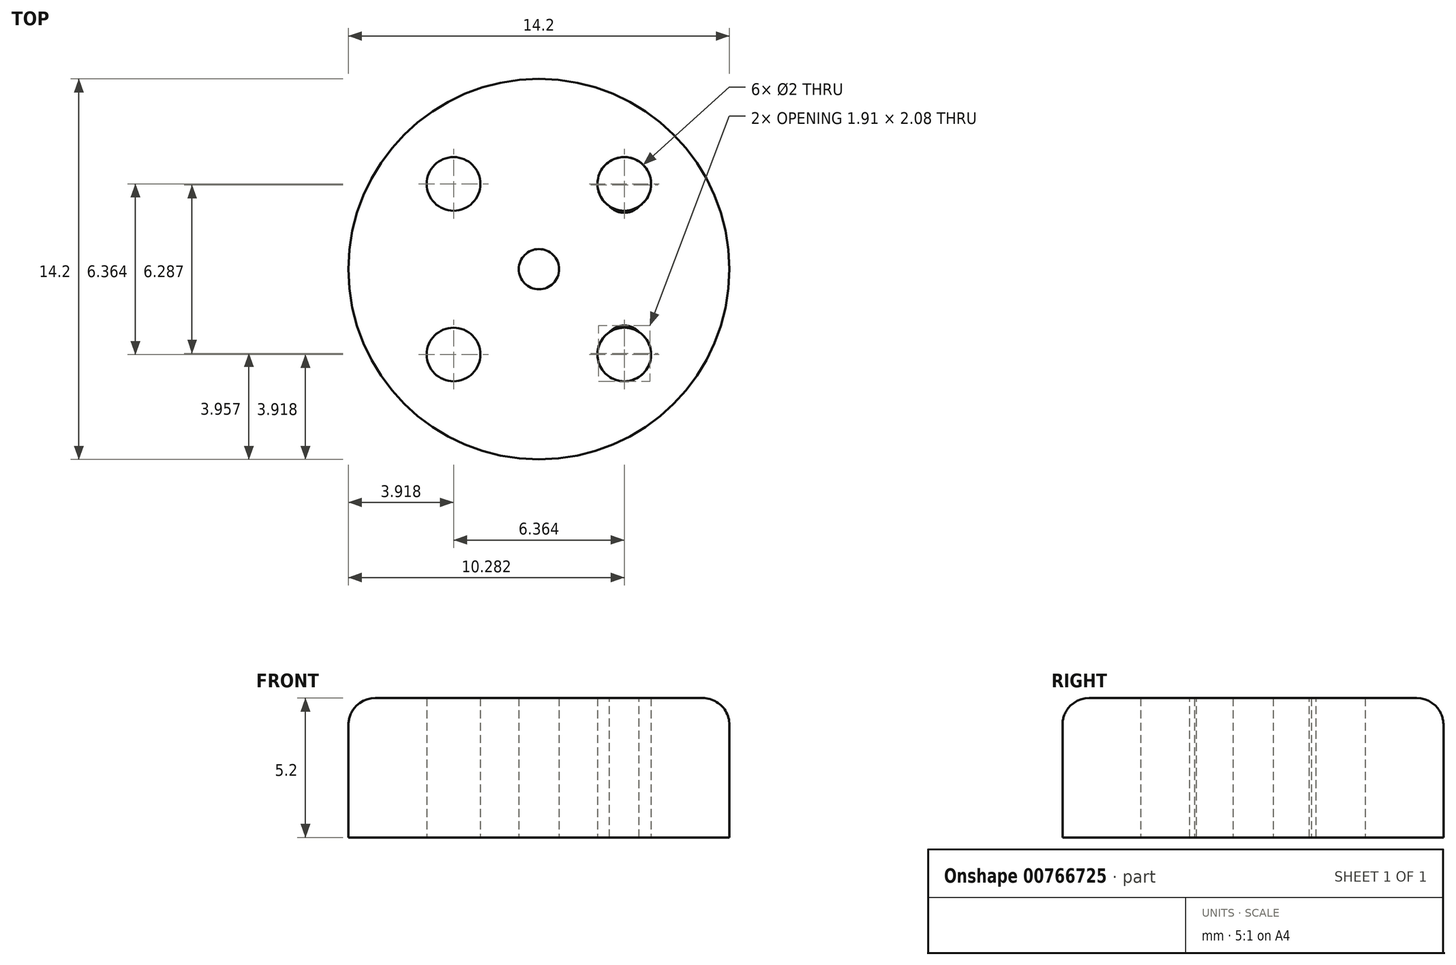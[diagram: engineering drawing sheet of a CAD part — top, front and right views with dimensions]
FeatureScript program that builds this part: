
annotation { "Feature Type Name" : "Feature", "Feature Type Description" : "" }
export const myFeature = defineFeature(function(context is Context, id is Id, definition is map)
    precondition{}
    {
        {
            var Q0;
            Q0=qCreatedBy(makeId("Top.planeOp"),FACE);
            var sketch = newSketch(context, id + "F0", { "sketchPlane" : qUnion([Q0])});
            skCircle(sketch, "E0", {"center": v(0, 0) * mm, "radius": 7.1 * mm});
            skCircle(sketch, "E1", {"center": v(0, 0) * mm, "radius": 0.75 * mm});
            skLineSegment(sketch, "E2.bottom", {"start": v(3.18, 3.18) * mm, "end": v(-3.18, 3.18) * mm, "construction": true});
            skLineSegment(sketch, "E2.top", {"start": v(3.18, -3.18) * mm, "end": v(-3.18, -3.18) * mm, "construction": true});
            skLineSegment(sketch, "E2.left", {"start": v(3.18, 3.18) * mm, "end": v(3.18, -3.18) * mm, "construction": true});
            skLineSegment(sketch, "E2.right", {"start": v(-3.18, 3.18) * mm, "end": v(-3.18, -3.18) * mm, "construction": true});
            skCircle(sketch, "E3", {"center": v(3.18, 3.18) * mm, "radius": 1 * mm});
            skCircle(sketch, "E4", {"center": v(3.18, -3.18) * mm, "radius": 1 * mm});
            skCircle(sketch, "E5", {"center": v(-3.18, -3.18) * mm, "radius": 1 * mm});
            skCircle(sketch, "E6", {"center": v(-3.18, 3.18) * mm, "radius": 1 * mm});
            skSolve(sketch);
        }
        {
            var Q0;
            Q0 = qSketchRegion(id + "F0", true);
            extrude(context, id + "F1", {"entities" : qUnion([Q0]), "depth" : 5.2 * mm, "offsetDistance" : 25 * mm});
        }
        {
            var Q0;
            Q0=makeQuery(id+"F1.opExtrude","CAP_EDGE",EDGE,{"disambiguationData":[OSD([sQuery(id+"F0.wireOp",EDGE,"E0")])],"isStart":false});
            fillet(context, id + "F2", {"entities" : qUnion([Q0]), "radius" : 1 * mm, "tangentPropagation" : true, "allowEdgeOverflow" : false});
        }
        {
            var Q0;
            Q0=qCreatedBy(makeId("Right.planeOp"),FACE);
            var sketch = newSketch(context, id + "F3", { "sketchPlane" : qUnion([Q0])});
            skLineSegment(sketch, "E7", {"start": v(-2.35, 4.95) * mm, "end": v(2.35, 0.25) * mm, "construction": true});
            skLineSegment(sketch, "E8", {"start": v(0, 5.2) * mm, "end": v(0, 0) * mm, "construction": true});
            skPoint(sketch, "E9", {"position": v(0, 2.6) * mm});
            skArc(sketch, "E10.0.startCap", {"start": v(-2.53, 4.77) * mm, "mid": v(-2.53, 5.13) * mm, "end": v(-2.17, 5.13) * mm});
            skArc(sketch, "E10.0.endCap", {"start": v(2.53, 0.43) * mm, "mid": v(2.53, 0.07) * mm, "end": v(2.17, 0.07) * mm});
            skLineSegment(sketch, "E10.0.left", {"start": v(-2.17, 5.13) * mm, "end": v(2.53, 0.43) * mm});
            skLineSegment(sketch, "E10.0.right", {"start": v(-2.53, 4.77) * mm, "end": v(2.17, 0.07) * mm});
            skSolve(sketch);
        }
        {
            var Q0;
            Q0 = qSketchRegion(id + "F3", true);
            extrude(context, id + "F4", {"entities" : qUnion([Q0]), "operationType" : NewBodyOperationType.ADD, "depth" : 2.3 / 50.8 * mm, "offsetDistance" : 25 * mm});
        }
        {
            var Q0;
            {var subQ0=sQuery(id+"F3.wireOp",EDGE,"E10.0.left");Q0=makeQuery(id+"F4.boolean.opBoolean","SPLIT",FACE,{"disambiguationData":[TD([makeQuery(id+"F1.opExtrude","SWEPT_FACE",FACE,{"disambiguationData":[OSD([sQuery(id+"F0.wireOp",EDGE,"E0")])]})])],"derivedFrom":makeQuery(id+"F4.opExtrude","SWEPT_FACE",FACE,{"disambiguationData":[OSD([subQ0])]})});}
            var sketch = newSketch(context, id + "F5", { "sketchPlane" : qUnion([Q0])});
            skLineSegment(sketch, "E11", {"start": v(29.21, -1.84) * mm, "end": v(15.18, -1.84) * mm, "construction": true});
            skLineSegment(sketch, "E12.0", {"start": v(29.21, 1.48) * mm, "end": v(29.21, 1.73) * mm});
            skLineSegment(sketch, "E13", {"start": v(29.21, 1.73) * mm, "end": v(26.83, 1.73) * mm});
            skArc(sketch, "E14", {"start": v(29.2, -0.65) * mm, "mid": v(28.51, 1.04) * mm, "end": v(26.83, 1.73) * mm});
            skLineSegment(sketch, "E15", {"start": v(29.21, 1.48) * mm, "end": v(29.21, -0.65) * mm});
            skLineSegment(sketch, "E16", {"start": v(29.21, -0.65) * mm, "end": v(29.21, -3.03) * mm, "construction": true});
            skArc(sketch, "E17.MirrorCS", {"start": v(29.2, -3.03) * mm, "mid": v(28.51, -4.71) * mm, "end": v(26.83, -5.41) * mm});
            skLineSegment(sketch, "E18.MirrorCS", {"start": v(29.21, -5.41) * mm, "end": v(26.83, -5.41) * mm});
            skLineSegment(sketch, "E19.MirrorCS", {"start": v(29.21, -5.16) * mm, "end": v(29.21, -5.41) * mm});
            skLineSegment(sketch, "E20.MirrorCS", {"start": v(29.21, -5.16) * mm, "end": v(29.21, -3.03) * mm});
            skSolve(sketch);
        }
        {
            var Q0;
            Q0 = qSketchRegion(id + "F5", true);
            extrude(context, id + "F6", {"entities" : qUnion([Q0]), "operationType" : NewBodyOperationType.REMOVE, "endBound" : BoundingType.THROUGH_ALL, "oppositeDirection" : true, "depth" : 25 * mm, "offsetDistance" : 25 * mm});
        }
        {
            var Q0;
            Q0=makeQuery(id+"F1.opExtrude","CAP_FACE",FACE,{"disambiguationData":[OSD([sQuery(id+"F0.wireOp",EDGE,"E0"),sQuery(id+"F0.wireOp",EDGE,"E1"),sQuery(id+"F0.wireOp",EDGE,"E3"),sQuery(id+"F0.wireOp",EDGE,"E4"),sQuery(id+"F0.wireOp",EDGE,"E5"),sQuery(id+"F0.wireOp",EDGE,"E6")])],"isStart":false});
            var sketch = newSketch(context, id + "F7", { "sketchPlane" : qUnion([Q0])});
            skCircle(sketch, "E21.0", {"center": v(-3.18, 3.18) * mm, "radius": 1 * mm});
            skCircle(sketch, "E21.1", {"center": v(3.18, 3.18) * mm, "radius": 1 * mm});
            skCircle(sketch, "E21.2", {"center": v(0, 0) * mm, "radius": 0.75 * mm});
            skArc(sketch, "E21.3", {"start": v(2.63, -2.35) * mm, "mid": v(3.18, -4.18) * mm, "end": v(3.74, -2.35) * mm});
            skCircle(sketch, "E21.4", {"center": v(-3.18, -3.18) * mm, "radius": 1 * mm});
            skArc(sketch, "E21.5", {"start": v(3.74, -2.35) * mm, "mid": v(3.18, -2.1) * mm, "end": v(2.63, -2.35) * mm});
            skSolve(sketch);
        }
        {
            var Q0;
            Q0 = qSketchRegion(id + "F7", true);
            extrude(context, id + "F8", {"entities" : qUnion([Q0]), "operationType" : NewBodyOperationType.REMOVE, "endBound" : BoundingType.THROUGH_ALL, "oppositeDirection" : true, "depth" : 25 * mm, "offsetDistance" : 25 * mm});
        }
        {
            var Q0;
            Q0=makeQuery(id+"F1.opExtrude","SWEPT_BODY",BODY,{"disambiguationData":[OSD([sQuery(id+"F0.wireOp",EDGE,"E0"),sQuery(id+"F0.wireOp",EDGE,"E1"),sQuery(id+"F0.wireOp",EDGE,"E3"),sQuery(id+"F0.wireOp",EDGE,"E4"),sQuery(id+"F0.wireOp",EDGE,"E5"),sQuery(id+"F0.wireOp",EDGE,"E6")])]});
            var Q1;
            Q1=qCreatedBy(makeId("Front.planeOp"),FACE);
            mirror(context, id + "F9", {"entities" : qUnion([Q0]), "mirrorPlane" : qUnion([Q1])});
        }
    });
